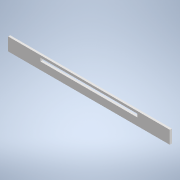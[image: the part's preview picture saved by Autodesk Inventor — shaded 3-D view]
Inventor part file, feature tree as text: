
AUTODESK INVENTOR PART (.ipt)
format: ipt  version: 2022 (Build 260153000, 153)  size: 117,760 bytes
history: native  units: mm
features: extrude x1, sketch x1
ambient origin geometry x8: Origin, YZ Plane, XZ Plane, XY Plane, X Axis, Y Axis, Z Axis, Center Point
bodies: Body1 (feature_tree)
feature tree (2):
  extrude  "Extrusion4"  Depth=20.0mm
  sketch  "Sketch1"  dims[d0=250.0mm d1=20.0mm d20=150.0mm d21=4.5mm d22=4.5mm d32=4.0mm d33=2.0mm d36=13.0mm d37=3.2mm d38=0.0mm]
